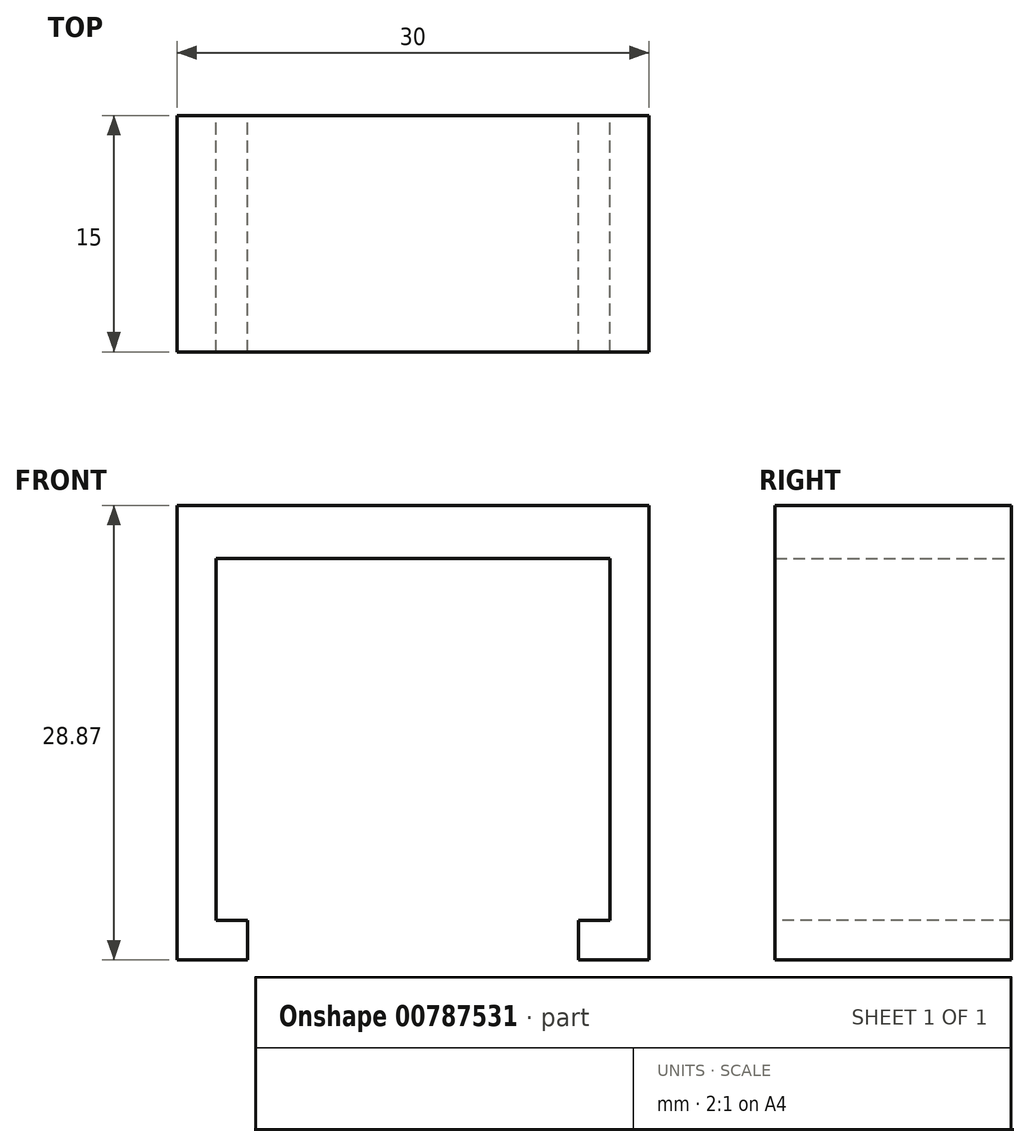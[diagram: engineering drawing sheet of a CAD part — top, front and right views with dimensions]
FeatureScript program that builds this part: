
annotation { "Feature Type Name" : "Feature", "Feature Type Description" : "" }
export const myFeature = defineFeature(function(context is Context, id is Id, definition is map)
    precondition{}
    {
        {
            var Q0;
            Q0=qCreatedBy(makeId("Top.planeOp"),FACE);
            var sketch = newSketch(context, id + "F0", { "sketchPlane" : qUnion([Q0])});
            skLineSegment(sketch, "E0.bottom", {"start": v(-35.66, -15.25) * mm, "end": v(-0.66, -15.25) * mm});
            skLineSegment(sketch, "E0.top", {"start": v(-35.66, -30.25) * mm, "end": v(-0.66, -30.25) * mm});
            skLineSegment(sketch, "E0.left", {"start": v(-35.66, -15.25) * mm, "end": v(-35.66, -30.25) * mm});
            skLineSegment(sketch, "E0.right", {"start": v(-0.66, -15.25) * mm, "end": v(-0.66, -30.25) * mm});
            skSolve(sketch);
        }
        {
            var Q0;
            Q0 = qSketchRegion(id + "F0", true);
            extrude(context, id + "F1", {"entities" : qUnion([Q0]), "oppositeDirection" : true, "depth" : 7.37 * mm, "offsetDistance" : 25.4 * mm});
        }
        {
            var Q0;
            Q0=makeQuery(id+"F1.opExtrude","CAP_FACE",FACE,{"disambiguationData":[OSD([sQuery(id+"F0.wireOp",EDGE,"E0.bottom"),sQuery(id+"F0.wireOp",EDGE,"E0.top"),sQuery(id+"F0.wireOp",EDGE,"E0.left"),sQuery(id+"F0.wireOp",EDGE,"E0.right")])],"isStart":false});
            var sketch = newSketch(context, id + "F2", { "sketchPlane" : qUnion([Q0])});
            skLineSegment(sketch, "E1.bottom", {"start": v(-35.66, 30.25) * mm, "end": v(-30.66, 30.25) * mm});
            skLineSegment(sketch, "E1.top", {"start": v(-35.66, 15.25) * mm, "end": v(-30.66, 15.25) * mm});
            skLineSegment(sketch, "E1.left", {"start": v(-35.66, 30.25) * mm, "end": v(-35.66, 15.25) * mm});
            skLineSegment(sketch, "E1.right", {"start": v(-30.66, 30.25) * mm, "end": v(-30.66, 15.25) * mm});
            skSolve(sketch);
        }
        {
            var Q0;
            Q0=makeQuery(id+"F2.imprint","IMPRINT",FACE,{"disambiguationData":[TD([[makeQuery(id+"F2.imprint","IMPRINT",EDGE,{"derivedFrom":sQuery(id+"F2.wireOp",EDGE,"E1.bottom")}),-1.0]])]});
            extrude(context, id + "F3", {"entities" : qUnion([Q0]), "operationType" : NewBodyOperationType.ADD, "depth" : 28 * mm, "offsetDistance" : 25 * mm});
        }
        {
            var Q0;
            Q0=makeQuery(id+"F1.opExtrude","CAP_FACE",FACE,{"disambiguationData":[OSD([sQuery(id+"F0.wireOp",EDGE,"E0.bottom"),sQuery(id+"F0.wireOp",EDGE,"E0.top"),sQuery(id+"F0.wireOp",EDGE,"E0.left"),sQuery(id+"F0.wireOp",EDGE,"E0.right")])],"isStart":false});
            var sketch = newSketch(context, id + "F4", { "sketchPlane" : qUnion([Q0])});
            skLineSegment(sketch, "E2.bottom", {"start": v(-0.66, 30.25) * mm, "end": v(-5.66, 30.25) * mm});
            skLineSegment(sketch, "E2.top", {"start": v(-0.66, 15.25) * mm, "end": v(-5.66, 15.25) * mm});
            skLineSegment(sketch, "E2.left", {"start": v(-0.66, 30.25) * mm, "end": v(-0.66, 15.25) * mm});
            skLineSegment(sketch, "E2.right", {"start": v(-5.66, 30.25) * mm, "end": v(-5.66, 15.25) * mm});
            skSolve(sketch);
        }
        {
            var Q0;
            Q0 = qSketchRegion(id + "F4", true);
            extrude(context, id + "F5", {"entities" : qUnion([Q0]), "operationType" : NewBodyOperationType.ADD, "depth" : 28 * mm, "offsetDistance" : 25 * mm});
        }
        {
            var Q0;
            Q0=makeQuery(id+"F5.opExtrude","SWEPT_FACE",FACE,{"disambiguationData":[OSD([sQuery(id+"F4.wireOp",EDGE,"E2.right")])]});
            var sketch = newSketch(context, id + "F6", { "sketchPlane" : qUnion([Q0])});
            skLineSegment(sketch, "E3.bottom", {"start": v(30.25, -35.37) * mm, "end": v(15.25, -35.37) * mm});
            skLineSegment(sketch, "E3.top", {"start": v(30.25, -30.37) * mm, "end": v(15.25, -30.37) * mm});
            skLineSegment(sketch, "E3.left", {"start": v(30.25, -35.37) * mm, "end": v(30.25, -30.37) * mm});
            skLineSegment(sketch, "E3.right", {"start": v(15.25, -35.37) * mm, "end": v(15.25, -30.37) * mm});
            skSolve(sketch);
        }
        {
            var Q0;
            Q0=makeQuery(id+"F3.opExtrude","SWEPT_FACE",FACE,{"disambiguationData":[OSD([sQuery(id+"F2.wireOp",EDGE,"E1.right")])]});
            var sketch = newSketch(context, id + "F7", { "sketchPlane" : qUnion([Q0])});
            skLineSegment(sketch, "E4.bottom", {"start": v(-15.25, -35.37) * mm, "end": v(-30.25, -35.37) * mm});
            skLineSegment(sketch, "E4.top", {"start": v(-15.25, -30.37) * mm, "end": v(-30.25, -30.37) * mm});
            skLineSegment(sketch, "E4.left", {"start": v(-15.25, -35.37) * mm, "end": v(-15.25, -30.37) * mm});
            skLineSegment(sketch, "E4.right", {"start": v(-30.25, -35.37) * mm, "end": v(-30.25, -30.37) * mm});
            skSolve(sketch);
        }
        {
            var Q0;
            Q0 = qSketchRegion(id + "F7", true);
            extrude(context, id + "F8", {"entities" : qUnion([Q0]), "operationType" : NewBodyOperationType.ADD, "depth" : 2 * mm, "offsetDistance" : 25 * mm});
        }
        {
            var Q0;
            Q0 = qSketchRegion(id + "F6", true);
            extrude(context, id + "F9", {"entities" : qUnion([Q0]), "operationType" : NewBodyOperationType.ADD, "depth" : 2 * mm, "offsetDistance" : 25 * mm});
        }
        {
            var Q0;
            Q0=makeQuery(id+"F1.opExtrude","CAP_FACE",FACE,{"disambiguationData":[OSD([sQuery(id+"F0.wireOp",EDGE,"E0.bottom"),sQuery(id+"F0.wireOp",EDGE,"E0.top"),sQuery(id+"F0.wireOp",EDGE,"E0.left"),sQuery(id+"F0.wireOp",EDGE,"E0.right")])],"isStart":true});
            extrude(context, id + "F10", {"entities" : qUnion([Q0]), "operationType" : NewBodyOperationType.REMOVE, "oppositeDirection" : true, "depth" : 4 * mm, "offsetDistance" : 25 * mm});
        }
        {
            var Q0;
            Q0=makeQuery(id+"F5.boolean.opBoolean","MERGE",FACE,{"derivedFrom":[makeQuery(id+"F1.opExtrude","SWEPT_FACE",FACE,{"disambiguationData":[OSD([sQuery(id+"F0.wireOp",EDGE,"E0.right")])]}),makeQuery(id+"F5.opExtrude","SWEPT_FACE",FACE,{"disambiguationData":[OSD([sQuery(id+"F4.wireOp",EDGE,"E2.left")])]})]});
            extrude(context, id + "F11", {"entities" : qUnion([Q0]), "operationType" : NewBodyOperationType.REMOVE, "oppositeDirection" : true, "depth" : 2.5 * mm, "offsetDistance" : 25 * mm});
        }
        {
            var Q0;
            Q0=makeQuery(id+"F3.boolean.opBoolean","MERGE",FACE,{"derivedFrom":[makeQuery(id+"F1.opExtrude","SWEPT_FACE",FACE,{"disambiguationData":[OSD([sQuery(id+"F0.wireOp",EDGE,"E0.left")])]}),makeQuery(id+"F3.opExtrude","SWEPT_FACE",FACE,{"disambiguationData":[OSD([sQuery(id+"F2.wireOp",EDGE,"E1.left")])]})]});
            extrude(context, id + "F12", {"entities" : qUnion([Q0]), "operationType" : NewBodyOperationType.REMOVE, "oppositeDirection" : true, "depth" : 2.5 * mm, "offsetDistance" : 25 * mm});
        }
        {
            var Q0;
            Q0=makeQuery(id+"F8.boolean.opBoolean","MERGE",FACE,{"derivedFrom":[makeQuery(id+"F3.opExtrude","CAP_FACE",FACE,{"disambiguationData":[OSD([sQuery(id+"F2.wireOp",EDGE,"E1.bottom"),sQuery(id+"F2.wireOp",EDGE,"E1.top"),sQuery(id+"F2.wireOp",EDGE,"E1.left"),sQuery(id+"F2.wireOp",EDGE,"E1.right")])],"isStart":false}),makeQuery(id+"F8.opExtrude","SWEPT_FACE",FACE,{"disambiguationData":[OSD([sQuery(id+"F7.wireOp",EDGE,"E4.bottom")])]})]});
            var Q1;
            Q1=makeQuery(id+"F9.boolean.opBoolean","MERGE",FACE,{"derivedFrom":[makeQuery(id+"F5.opExtrude","CAP_FACE",FACE,{"disambiguationData":[OSD([sQuery(id+"F4.wireOp",EDGE,"E2.bottom"),sQuery(id+"F4.wireOp",EDGE,"E2.top"),sQuery(id+"F4.wireOp",EDGE,"E2.left"),sQuery(id+"F4.wireOp",EDGE,"E2.right")])],"isStart":false}),makeQuery(id+"F9.opExtrude","SWEPT_FACE",FACE,{"disambiguationData":[OSD([sQuery(id+"F6.wireOp",EDGE,"E3.bottom")])]})]});
            extrude(context, id + "F13", {"entities" : qUnion([Q0, Q1]), "operationType" : NewBodyOperationType.REMOVE, "oppositeDirection" : true, "depth" : 2.5 * mm, "offsetDistance" : 25 * mm});
        }
    });
